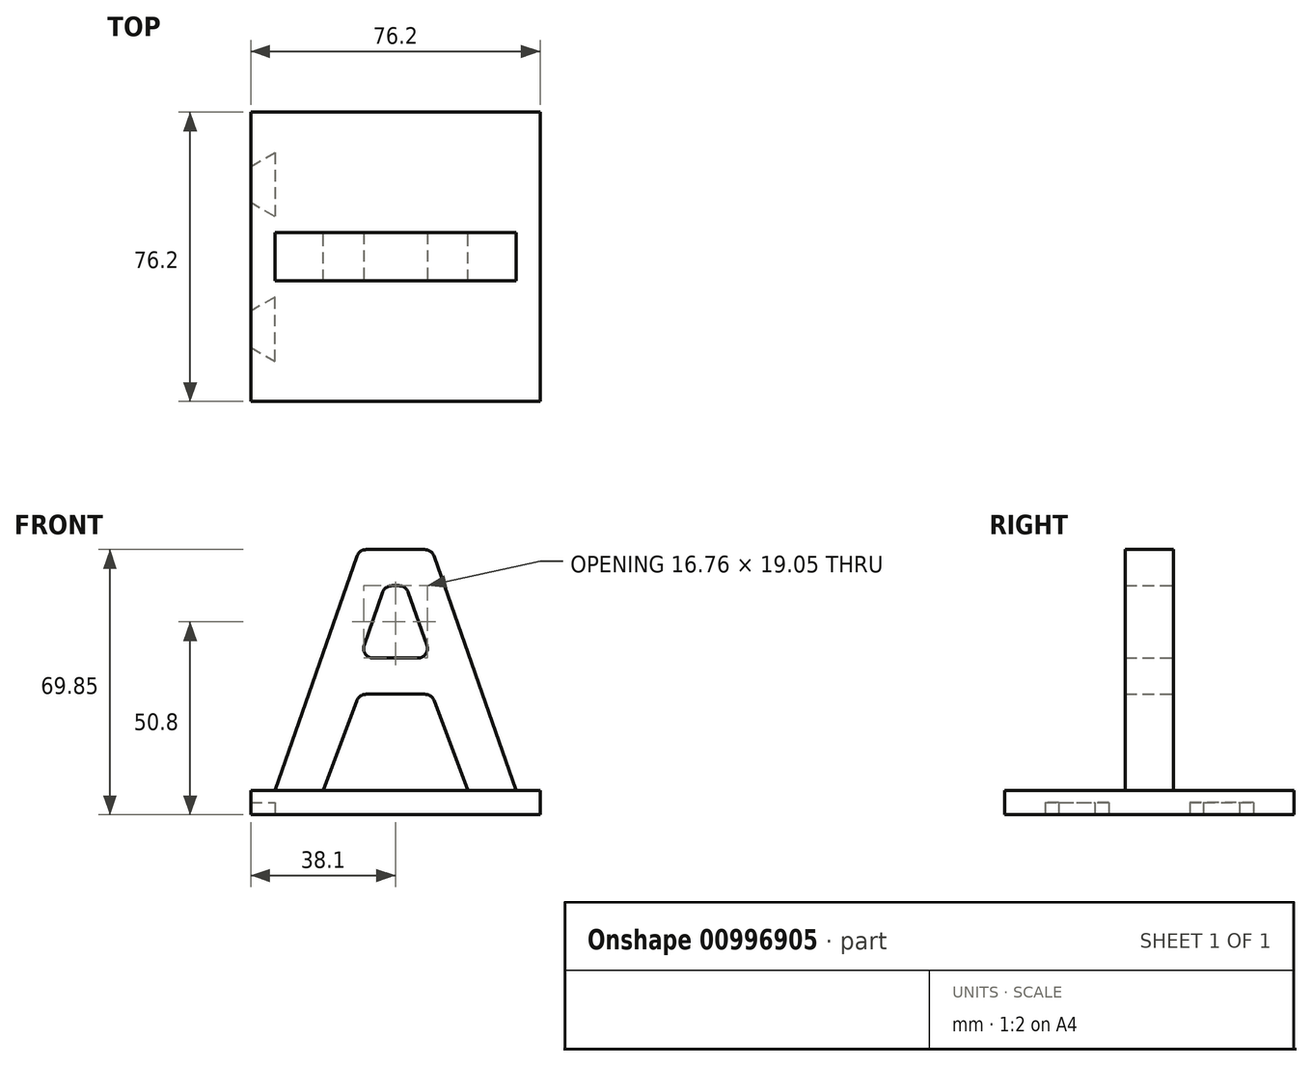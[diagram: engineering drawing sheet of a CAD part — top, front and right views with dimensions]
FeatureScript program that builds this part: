
annotation { "Feature Type Name" : "Feature", "Feature Type Description" : "" }
export const myFeature = defineFeature(function(context is Context, id is Id, definition is map)
    precondition{}
    {
        {
            var Q0;
            Q0=qCreatedBy(makeId("Top.planeOp"),FACE);
            var sketch = newSketch(context, id + "F0", { "sketchPlane" : qUnion([Q0])});
            skLineSegment(sketch, "E0.bottom", {"start": v(38.1, -38.1) * mm, "end": v(-38.1, -38.1) * mm});
            skLineSegment(sketch, "E0.top", {"start": v(38.1, 38.1) * mm, "end": v(-38.1, 38.1) * mm});
            skLineSegment(sketch, "E0.left", {"start": v(38.1, -38.1) * mm, "end": v(38.1, 38.1) * mm});
            skLineSegment(sketch, "E0.right", {"start": v(-38.1, -38.1) * mm, "end": v(-38.1, 38.1) * mm});
            skPoint(sketch, "E0.middle", {"position": v(0, 0) * mm});
            skSolve(sketch);
        }
        {
            var Q0;
            Q0=qCreatedBy(makeId("Front.planeOp"),FACE);
            var sketch = newSketch(context, id + "F1", { "sketchPlane" : qUnion([Q0])});
            skLineSegment(sketch, "E1", {"start": v(31.75, 0) * mm, "end": v(9.53, 63.5) * mm});
            skLineSegment(sketch, "E2", {"start": v(9.53, 63.5) * mm, "end": v(-9.52, 63.5) * mm});
            skLineSegment(sketch, "E3", {"start": v(-9.52, 63.5) * mm, "end": v(-31.75, 0) * mm});
            skLineSegment(sketch, "E4", {"start": v(-31.75, 0) * mm, "end": v(-19.05, 0) * mm});
            skLineSegment(sketch, "E5", {"start": v(19.05, 0) * mm, "end": v(31.75, 0) * mm});
            skLineSegment(sketch, "E6", {"start": v(9.43, 34.92) * mm, "end": v(-9.43, 34.92) * mm});
            skLineSegment(sketch, "E7", {"start": v(-9.43, 34.92) * mm, "end": v(-2.77, 53.98) * mm});
            skLineSegment(sketch, "E8", {"start": v(-2.77, 53.98) * mm, "end": v(2.77, 53.98) * mm});
            skLineSegment(sketch, "E9", {"start": v(2.77, 53.98) * mm, "end": v(9.43, 34.92) * mm});
            skLineSegment(sketch, "E10", {"start": v(19.05, 0) * mm, "end": v(9.53, 25.4) * mm});
            skLineSegment(sketch, "E11", {"start": v(9.53, 25.4) * mm, "end": v(-9.52, 25.4) * mm});
            skLineSegment(sketch, "E12", {"start": v(-9.52, 25.4) * mm, "end": v(-19.05, 0) * mm});
            skSolve(sketch);
        }
        {
            var Q0;
            Q0 = qSketchRegion(id + "F0", true);
            extrude(context, id + "F2", {"entities" : qUnion([Q0]), "oppositeDirection" : true, "depth" : 6.35 * mm, "offsetDistance" : 25.4 * mm});
        }
        {
            var Q0;
            Q0 = qSketchRegion(id + "F1", true);
            extrude(context, id + "F3", {"entities" : qUnion([Q0]), "operationType" : NewBodyOperationType.ADD, "endBound" : BoundingType.SYMMETRIC, "depth" : 12.7 * mm, "offsetDistance" : 25.4 * mm});
        }
        {
            var Q0;
            Q0=makeQuery(id+"F3.opExtrude","CAP_EDGE",EDGE,{"disambiguationData":[OSD([sQuery(id+"F1.wireOp",EDGE,"E5")])],"isStart":true});
            var Q1;
            Q1=makeQuery(id+"F3.opExtrude","SWEPT_EDGE",EDGE,{"disambiguationData":[OSD([sQuery(id+"F1.wireOp",EDGE,"E5"),sQuery(id+"F1.wireOp",EDGE,"E10")])]});
            var Q2;
            Q2=makeQuery(id+"F3.opExtrude","SWEPT_EDGE",EDGE,{"disambiguationData":[OSD([sQuery(id+"F1.wireOp",EDGE,"E1"),sQuery(id+"F1.wireOp",EDGE,"E5")])]});
            var Q3;
            Q3=makeQuery(id+"F3.opExtrude","CAP_EDGE",EDGE,{"disambiguationData":[OSD([sQuery(id+"F1.wireOp",EDGE,"E5")])],"isStart":false});
            var Q4;
            Q4=makeQuery(id+"F3.opExtrude","CAP_EDGE",EDGE,{"disambiguationData":[OSD([sQuery(id+"F1.wireOp",EDGE,"E4")])],"isStart":false});
            var Q5;
            Q5=makeQuery(id+"F3.opExtrude","SWEPT_EDGE",EDGE,{"disambiguationData":[OSD([sQuery(id+"F1.wireOp",EDGE,"E4"),sQuery(id+"F1.wireOp",EDGE,"E12")])]});
            var Q6;
            Q6=makeQuery(id+"F3.opExtrude","CAP_EDGE",EDGE,{"disambiguationData":[OSD([sQuery(id+"F1.wireOp",EDGE,"E4")])],"isStart":true});
            var Q7;
            Q7=makeQuery(id+"F3.opExtrude","SWEPT_EDGE",EDGE,{"disambiguationData":[OSD([sQuery(id+"F1.wireOp",EDGE,"E3"),sQuery(id+"F1.wireOp",EDGE,"E4")])]});
            var Q8;
            Q8=makeQuery(id+"F3.opExtrude","SWEPT_EDGE",EDGE,{"disambiguationData":[OSD([sQuery(id+"F1.wireOp",EDGE,"E6"),sQuery(id+"F1.wireOp",EDGE,"E9")])]});
            var Q9;
            Q9=makeQuery(id+"F3.opExtrude","SWEPT_EDGE",EDGE,{"disambiguationData":[OSD([sQuery(id+"F1.wireOp",EDGE,"E6"),sQuery(id+"F1.wireOp",EDGE,"E7")])]});
            var Q10;
            Q10=makeQuery(id+"F3.opExtrude","SWEPT_EDGE",EDGE,{"disambiguationData":[OSD([sQuery(id+"F1.wireOp",EDGE,"E8"),sQuery(id+"F1.wireOp",EDGE,"E9")])]});
            var Q11;
            Q11=makeQuery(id+"F3.opExtrude","SWEPT_EDGE",EDGE,{"disambiguationData":[OSD([sQuery(id+"F1.wireOp",EDGE,"E7"),sQuery(id+"F1.wireOp",EDGE,"E8")])]});
            var Q12;
            Q12=makeQuery(id+"F3.opExtrude","SWEPT_EDGE",EDGE,{"disambiguationData":[OSD([sQuery(id+"F1.wireOp",EDGE,"E1"),sQuery(id+"F1.wireOp",EDGE,"E2")])]});
            var Q13;
            Q13=makeQuery(id+"F3.opExtrude","SWEPT_EDGE",EDGE,{"disambiguationData":[OSD([sQuery(id+"F1.wireOp",EDGE,"E2"),sQuery(id+"F1.wireOp",EDGE,"E3")])]});
            var Q14;
            Q14=makeQuery(id+"F3.opExtrude","SWEPT_EDGE",EDGE,{"disambiguationData":[OSD([sQuery(id+"F1.wireOp",EDGE,"E10"),sQuery(id+"F1.wireOp",EDGE,"E11")])]});
            var Q15;
            Q15=makeQuery(id+"F3.opExtrude","SWEPT_EDGE",EDGE,{"disambiguationData":[OSD([sQuery(id+"F1.wireOp",EDGE,"E11"),sQuery(id+"F1.wireOp",EDGE,"E12")])]});
            fillet(context, id + "F4", {"entities" : qUnion([Q0, Q1, Q2, Q3, Q4, Q5, Q6, Q7, Q8, Q9, Q10, Q11, Q12, Q13, Q14, Q15]), "radius" : 2.54 * mm, "tangentPropagation" : true, "allowEdgeOverflow" : false});
        }
        {
            var Q0;
            Q0=makeQuery(id+"F2.opExtrude","CAP_FACE",FACE,{"disambiguationData":[OSD([sQuery(id+"F0.wireOp",EDGE,"E0.bottom"),sQuery(id+"F0.wireOp",EDGE,"E0.top"),sQuery(id+"F0.wireOp",EDGE,"E0.left"),sQuery(id+"F0.wireOp",EDGE,"E0.right")])],"isStart":false});
            var sketch = newSketch(context, id + "F5", { "sketchPlane" : qUnion([Q0])});
            skLineSegment(sketch, "E13", {"start": v(-38.1, -23.81) * mm, "end": v(-31.75, -27.48) * mm});
            skLineSegment(sketch, "E14", {"start": v(-31.75, -27.48) * mm, "end": v(-31.75, -10.62) * mm});
            skLineSegment(sketch, "E15", {"start": v(-31.75, -10.62) * mm, "end": v(-38.1, -14.29) * mm});
            skLineSegment(sketch, "E16", {"start": v(-38.1, -14.29) * mm, "end": v(-38.1, -23.81) * mm});
            skLineSegment(sketch, "E17", {"start": v(-38.1, -38.1) * mm, "end": v(-38.1, -19.05) * mm, "construction": true});
            skLineSegment(sketch, "E18.MirrorCS", {"start": v(-38.1, 23.81) * mm, "end": v(-31.75, 27.48) * mm});
            skLineSegment(sketch, "E19.MirrorCS", {"start": v(-31.75, 27.48) * mm, "end": v(-31.75, 10.62) * mm});
            skLineSegment(sketch, "E20.MirrorCS", {"start": v(-38.1, 14.29) * mm, "end": v(-38.1, 23.81) * mm});
            skLineSegment(sketch, "E21.MirrorCS", {"start": v(-31.75, 10.62) * mm, "end": v(-38.1, 14.29) * mm});
            skSolve(sketch);
        }
        {
            var Q0;
            Q0 = qSketchRegion(id + "F5", true);
            extrude(context, id + "F6", {"entities" : qUnion([Q0]), "operationType" : NewBodyOperationType.REMOVE, "oppositeDirection" : true, "depth" : 3.17 * mm, "offsetDistance" : 25.4 * mm});
        }
    });
